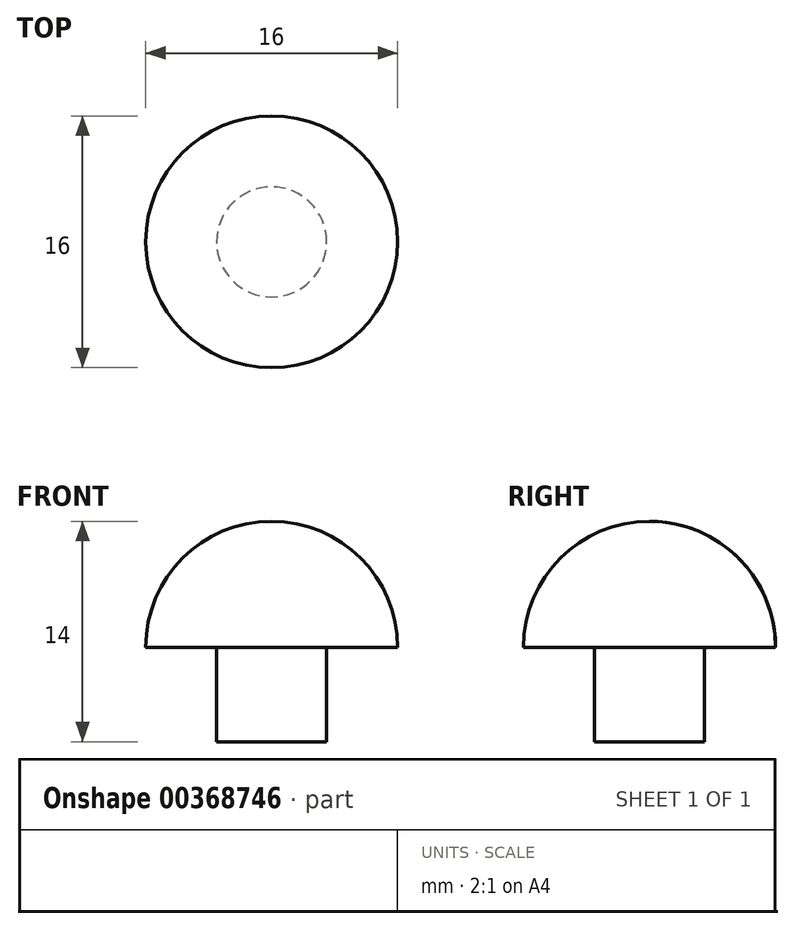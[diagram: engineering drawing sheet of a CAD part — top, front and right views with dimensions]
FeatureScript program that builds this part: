
annotation { "Feature Type Name" : "Feature", "Feature Type Description" : "" }
export const myFeature = defineFeature(function(context is Context, id is Id, definition is map)
    precondition{}
    {
        {
            var Q0;
            Q0=qCreatedBy(makeId("Top.planeOp"),FACE);
            var sketch = newSketch(context, id + "F0", { "sketchPlane" : qUnion([Q0])});
            skCircle(sketch, "E0", {"center": v(0, 0) * mm, "radius": 3.5 * mm});
            skCircle(sketch, "E1", {"center": v(0, 0) * mm, "radius": 8 * mm});
            skSolve(sketch);
        }
        {
            var Q0;
            Q0=qCreatedBy(makeId("Right.planeOp"),FACE);
            var sketch = newSketch(context, id + "F1", { "sketchPlane" : qUnion([Q0])});
            skCircle(sketch, "E2", {"center": v(0, 0) * mm, "radius": 8 * mm});
            skLineSegment(sketch, "E3", {"start": v(8, 0) * mm, "end": v(-8, 0) * mm});
            skLineSegment(sketch, "E4", {"start": v(0, 0) * mm, "end": v(0, 8) * mm});
            skLineSegment(sketch, "E5", {"start": v(0, -20.05) * mm, "end": v(0, 24.32) * mm, "construction": true});
            skSolve(sketch);
        }
        {
            var Q0;
            Q0=makeQuery(id+"F0.imprint","IMPRINT",FACE,{"disambiguationData":[TD([[makeQuery(id+"F0.imprint","IMPRINT",EDGE,{"derivedFrom":sQuery(id+"F0.wireOp",EDGE,"E0")}),1.0]])]});
            extrude(context, id + "F2", {"entities" : qUnion([Q0]), "oppositeDirection" : true, "depth" : 6 * mm});
        }
        {
            var Q0;
            {var subQ3=sQuery(id+"F1.wireOp",EDGE,"E4");Q0=makeQuery(id+"F1.imprint","IMPRINT",FACE,{"disambiguationData":[TD([[makeQuery(id+"F1.imprint","IMPRINT",EDGE,{"derivedFrom":subQ3}),1.0]])]});}
            var Q1;
            Q1=sQuery(id+"F1.wireOp",EDGE,"E5");
            revolve(context, id + "F3", {"operationType" : NewBodyOperationType.ADD, "entities" : qUnion([Q0]), "axis" : qUnion([Q1]), "revolveType" : RevolveType.FULL});
        }
    });
